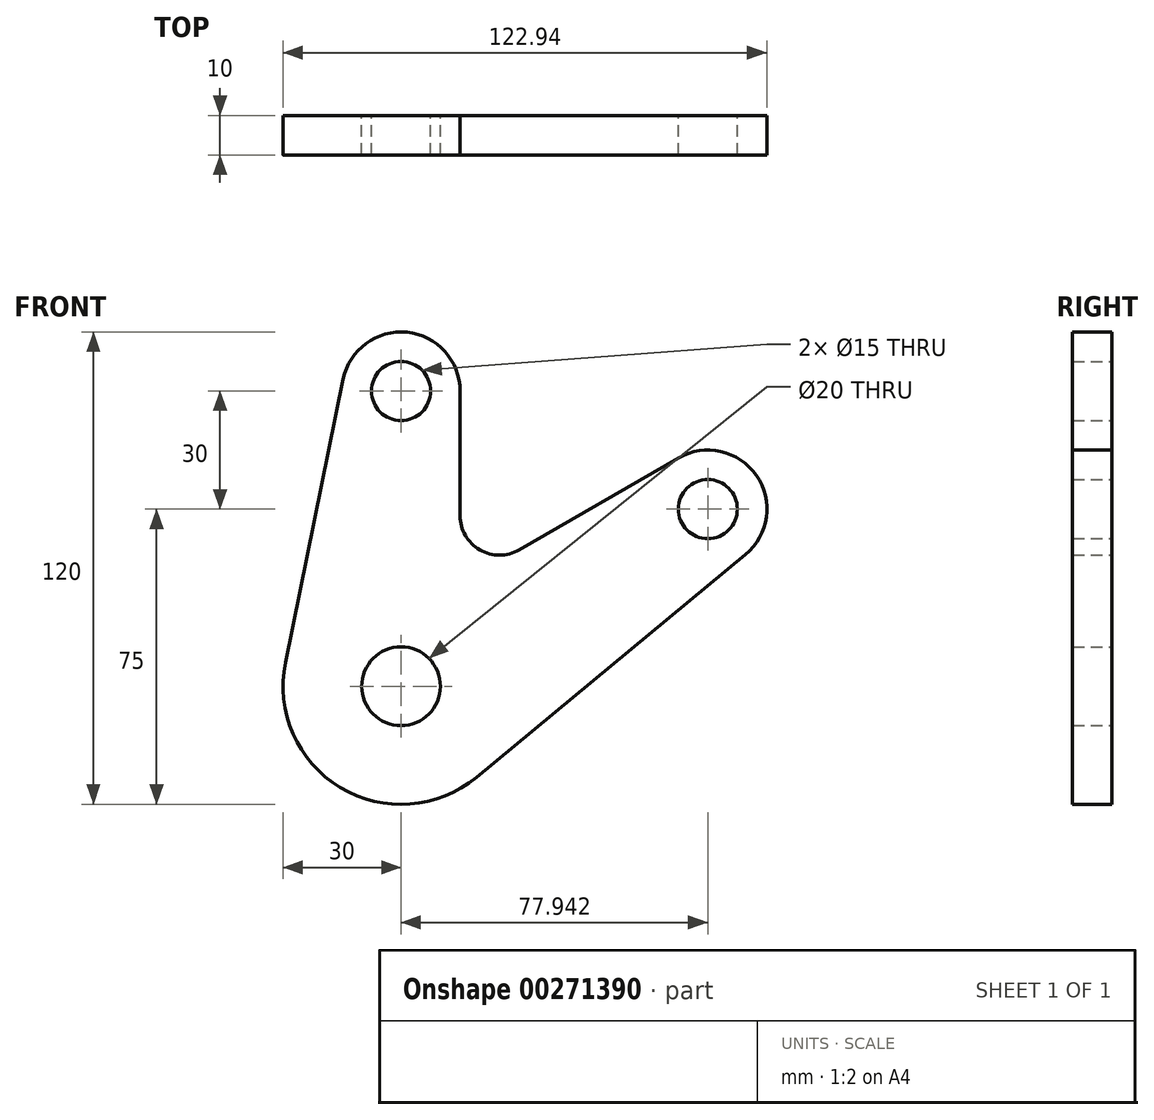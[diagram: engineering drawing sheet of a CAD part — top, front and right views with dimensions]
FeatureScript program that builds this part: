
annotation { "Feature Type Name" : "Feature", "Feature Type Description" : "" }
export const myFeature = defineFeature(function(context is Context, id is Id, definition is map)
    precondition{}
    {
        {
            var Q0;
            Q0=qCreatedBy(makeId("Front.planeOp"),FACE);
            var sketch = newSketch(context, id + "F0", { "sketchPlane" : qUnion([Q0])});
            skCircle(sketch, "E0", {"center": v(0, 0) * mm, "radius": 10 * mm});
            skCircle(sketch, "E1", {"center": v(77.94, 45) * mm, "radius": 7.5 * mm});
            skCircle(sketch, "E2", {"center": v(0, 75) * mm, "radius": 7.5 * mm});
            skArc(sketch, "E3", {"start": v(-29.4, 6) * mm, "mid": v(-15.44, -25.72) * mm, "end": v(19.12, -23.12) * mm});
            skLineSegment(sketch, "E4", {"start": v(-29.4, 6) * mm, "end": v(-14.7, 78) * mm});
            skArc(sketch, "E5", {"start": v(15, 75) * mm, "mid": v(1.5, 89.92) * mm, "end": v(-14.7, 78) * mm});
            skArc(sketch, "E6", {"start": v(15, 43.3) * mm, "mid": v(20, 34.64) * mm, "end": v(30, 34.64) * mm});
            skArc(sketch, "E7", {"start": v(87.5, 33.44) * mm, "mid": v(90.26, 53.56) * mm, "end": v(70.44, 58) * mm});
            skLineSegment(sketch, "E8", {"start": v(19.12, -23.12) * mm, "end": v(87.5, 33.44) * mm});
            skLineSegment(sketch, "E9", {"start": v(30, 34.64) * mm, "end": v(70.44, 58) * mm});
            skLineSegment(sketch, "E10", {"start": v(15, 75) * mm, "end": v(15, 43.3) * mm});
            skLineSegment(sketch, "E11", {"start": v(0, 75) * mm, "end": v(0, 0) * mm, "construction": true});
            skLineSegment(sketch, "E12", {"start": v(0, 0) * mm, "end": v(77.94, 45) * mm, "construction": true});
            skSolve(sketch);
        }
        {
            var Q0;
            Q0 = qSketchRegion(id + "F0", true);
            extrude(context, id + "F1", {"entities" : qUnion([Q0]), "depth" : 10 * mm});
        }
    });
